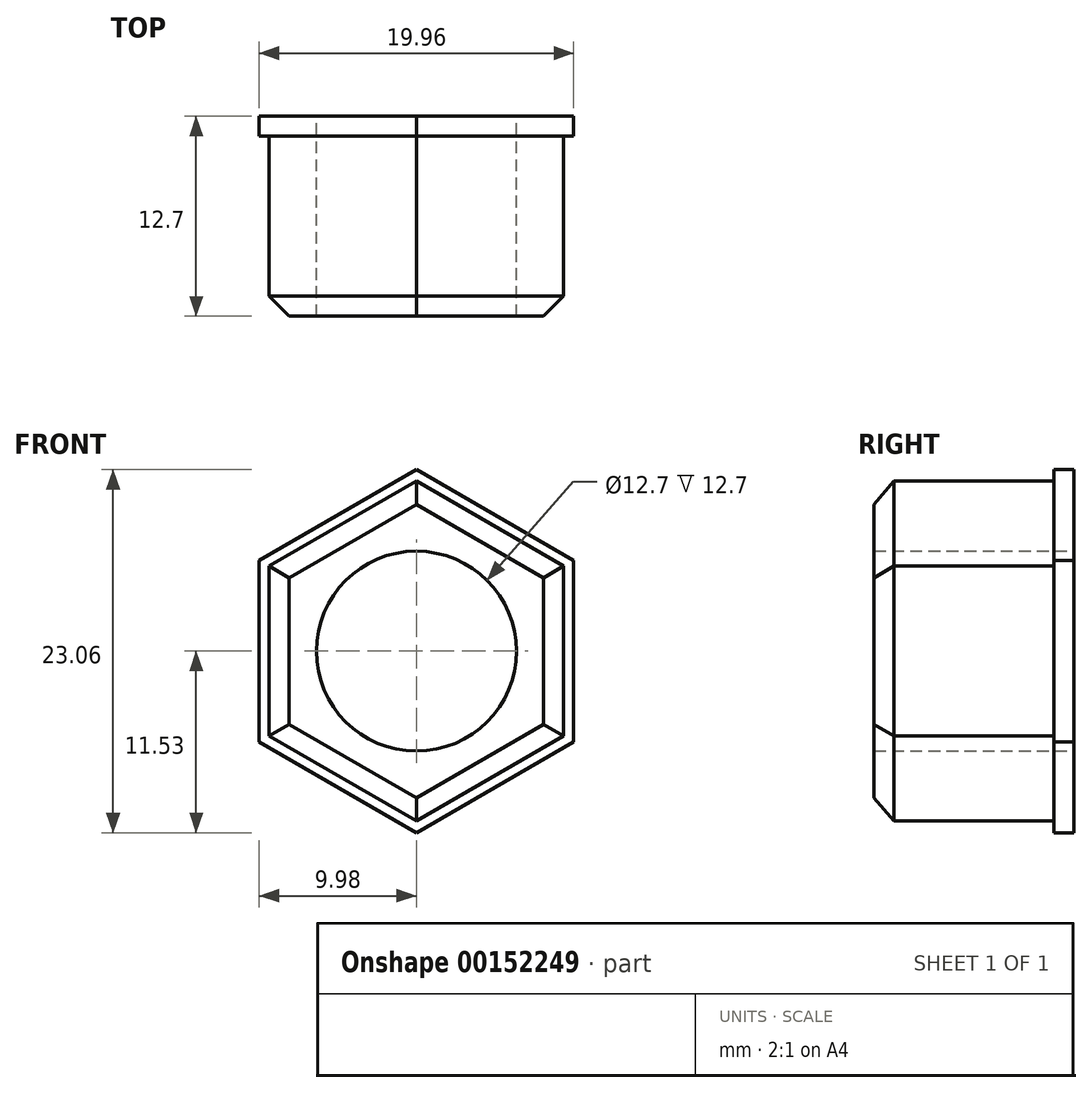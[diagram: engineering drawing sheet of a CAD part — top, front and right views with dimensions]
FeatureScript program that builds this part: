
annotation { "Feature Type Name" : "Feature", "Feature Type Description" : "" }
export const myFeature = defineFeature(function(context is Context, id is Id, definition is map)
    precondition{}
    {
        {
            var Q0;
            Q0=qCreatedBy(makeId("Front.planeOp"),FACE);
            var sketch = newSketch(context, id + "F0", { "sketchPlane" : qUnion([Q0])});
            skCircle(sketch, "E0", {"center": v(0, 0) * mm, "radius": 6.35 * mm});
            skLineSegment(sketch, "E1.0", {"start": v(0, 10.8) * mm, "end": v(9.35, 5.4) * mm});
            skLineSegment(sketch, "E1.1", {"start": v(9.35, 5.4) * mm, "end": v(9.35, -5.4) * mm});
            skLineSegment(sketch, "E1.2", {"start": v(9.35, -5.4) * mm, "end": v(0, -10.8) * mm});
            skLineSegment(sketch, "E1.3", {"start": v(0, -10.8) * mm, "end": v(-9.35, -5.4) * mm});
            skLineSegment(sketch, "E1.4", {"start": v(-9.35, -5.4) * mm, "end": v(-9.35, 5.4) * mm});
            skLineSegment(sketch, "E1.5", {"start": v(-9.35, 5.4) * mm, "end": v(0, 10.8) * mm});
            skSolve(sketch);
        }
        {
            var Q0;
            Q0=makeQuery(id+"F0.imprint","IMPRINT",FACE,{"disambiguationData":[TD([[makeQuery(id+"F0.imprint","IMPRINT",EDGE,{"derivedFrom":sQuery(id+"F0.wireOp",EDGE,"E0")}),-1.0]])]});
            extrude(context, id + "F1", {"entities" : qUnion([Q0]), "depth" : 12.7 * mm});
        }
        {
            var Q0;
            Q0=makeQuery(id+"F1.opExtrude","CAP_EDGE",EDGE,{"disambiguationData":[OSD([sQuery(id+"F0.wireOp",EDGE,"E1.0")])],"isStart":false});
            var Q1;
            Q1=makeQuery(id+"F1.opExtrude","CAP_EDGE",EDGE,{"disambiguationData":[OSD([sQuery(id+"F0.wireOp",EDGE,"E1.1")])],"isStart":false});
            var Q2;
            Q2=makeQuery(id+"F1.opExtrude","CAP_EDGE",EDGE,{"disambiguationData":[OSD([sQuery(id+"F0.wireOp",EDGE,"E1.2")])],"isStart":false});
            var Q3;
            Q3=makeQuery(id+"F1.opExtrude","CAP_EDGE",EDGE,{"disambiguationData":[OSD([sQuery(id+"F0.wireOp",EDGE,"E1.3")])],"isStart":false});
            var Q4;
            Q4=makeQuery(id+"F1.opExtrude","CAP_EDGE",EDGE,{"disambiguationData":[OSD([sQuery(id+"F0.wireOp",EDGE,"E1.4")])],"isStart":false});
            var Q5;
            Q5=makeQuery(id+"F1.opExtrude","CAP_EDGE",EDGE,{"disambiguationData":[OSD([sQuery(id+"F0.wireOp",EDGE,"E1.5")])],"isStart":false});
            chamfer(context, id + "F2", {"entities" : qUnion([Q0, Q1, Q2, Q3, Q4, Q5]), "width" : 1.27 * mm, "tangentPropagation" : true});
        }
        {
            var Q0;
            Q0=makeQuery(id+"F1.opExtrude","CAP_FACE",FACE,{"disambiguationData":[OSD([sQuery(id+"F0.wireOp",EDGE,"E0"),sQuery(id+"F0.wireOp",EDGE,"E1.0"),sQuery(id+"F0.wireOp",EDGE,"E1.1"),sQuery(id+"F0.wireOp",EDGE,"E1.2"),sQuery(id+"F0.wireOp",EDGE,"E1.3"),sQuery(id+"F0.wireOp",EDGE,"E1.4"),sQuery(id+"F0.wireOp",EDGE,"E1.5")])],"isStart":true});
            var sketch = newSketch(context, id + "F3", { "sketchPlane" : qUnion([Q0])});
            skLineSegment(sketch, "E2.0", {"start": v(-9.35, 5.4) * mm, "end": v(-9.35, -5.4) * mm});
            skLineSegment(sketch, "E3.0", {"start": v(0, 10.8) * mm, "end": v(-9.35, 5.4) * mm});
            skLineSegment(sketch, "E4.0", {"start": v(9.35, 5.4) * mm, "end": v(0, 10.8) * mm});
            skLineSegment(sketch, "E5.0", {"start": v(9.35, -5.4) * mm, "end": v(9.35, 5.4) * mm});
            skLineSegment(sketch, "E6.0", {"start": v(0, -10.8) * mm, "end": v(9.35, -5.4) * mm});
            skLineSegment(sketch, "E7.0", {"start": v(-9.35, -5.4) * mm, "end": v(0, -10.8) * mm});
            skCircle(sketch, "E8.0", {"center": v(0, 0) * mm, "radius": 6.35 * mm});
            skLineSegment(sketch, "E9.0", {"start": v(9.98, 5.76) * mm, "end": v(0, 11.53) * mm});
            skLineSegment(sketch, "E9.1", {"start": v(-9.98, 5.76) * mm, "end": v(-9.98, -5.76) * mm});
            skLineSegment(sketch, "E9.2", {"start": v(-9.98, -5.76) * mm, "end": v(0, -11.53) * mm});
            skLineSegment(sketch, "E9.3", {"start": v(0, 11.53) * mm, "end": v(-9.98, 5.76) * mm});
            skLineSegment(sketch, "E9.4", {"start": v(0, -11.53) * mm, "end": v(9.98, -5.76) * mm});
            skLineSegment(sketch, "E9.5", {"start": v(9.98, -5.76) * mm, "end": v(9.98, 5.76) * mm});
            skSolve(sketch);
        }
        {
            var Q0;
            Q0=makeQuery(id+"F3.imprint","IMPRINT",FACE,{"disambiguationData":[TD([[makeQuery(id+"F3.imprint","IMPRINT",EDGE,{"derivedFrom":sQuery(id+"F3.wireOp",EDGE,"E2.0")}),-1.0]])]});
            extrude(context, id + "F4", {"entities" : qUnion([Q0]), "operationType" : NewBodyOperationType.ADD, "oppositeDirection" : true, "depth" : 1.27 * mm});
        }
    });
